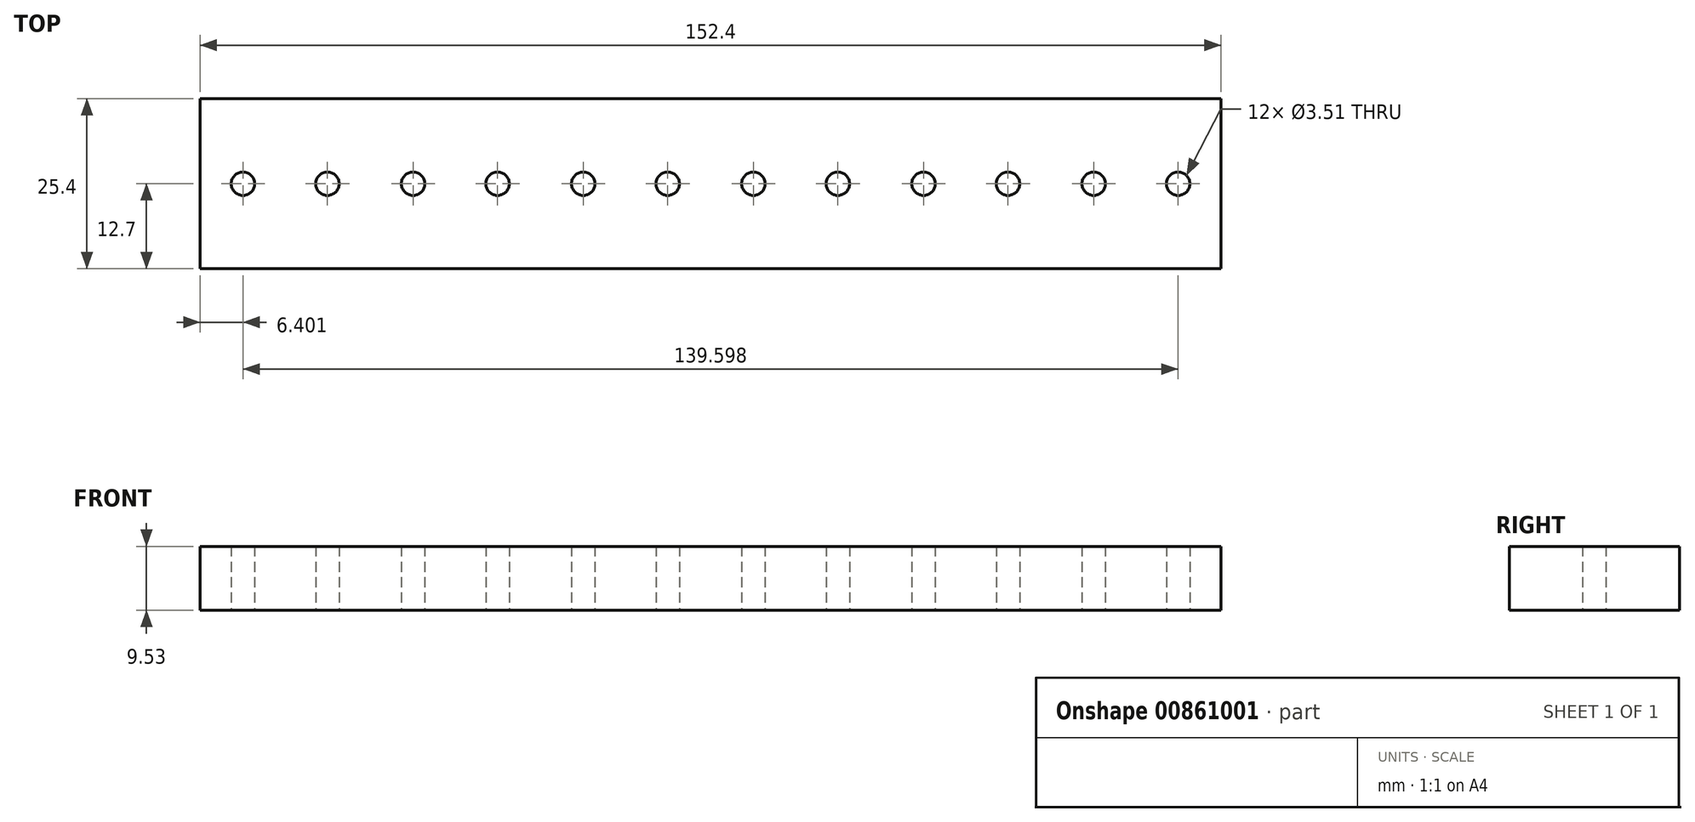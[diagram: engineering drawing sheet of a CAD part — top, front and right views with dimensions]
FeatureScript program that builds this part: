
annotation { "Feature Type Name" : "Feature", "Feature Type Description" : "" }
export const myFeature = defineFeature(function(context is Context, id is Id, definition is map)
    precondition{}
    {
        {
            var Q0;
            Q0=qCreatedBy(makeId("Top.planeOp"),FACE);
            var sketch = newSketch(context, id + "F0", { "sketchPlane" : qUnion([Q0])});
            skLineSegment(sketch, "E0.bottom", {"start": v(0, 0) * mm, "end": v(152.4, 0) * mm});
            skLineSegment(sketch, "E0.top", {"start": v(0, 25.4) * mm, "end": v(152.4, 25.4) * mm});
            skLineSegment(sketch, "E0.left", {"start": v(0, 0) * mm, "end": v(0, 25.4) * mm});
            skLineSegment(sketch, "E0.right", {"start": v(152.4, 0) * mm, "end": v(152.4, 25.4) * mm});
            skLineSegment(sketch, "E1", {"start": v(12.7, 25.4) * mm, "end": v(12.7, 0) * mm, "construction": true});
            skLineSegment(sketch, "E2", {"start": v(0, 12.7) * mm, "end": v(152.4, 12.7) * mm, "construction": true});
            skCircle(sketch, "E3", {"center": v(6.4, 12.7) * mm, "radius": 1.75 * mm});
            skLineSegment(sketch, "E4.direction1", {"start": v(6.4, 12.7) * mm, "end": v(19.2, 12.7) * mm, "construction": true});
            skCircle(sketch, "E5.MirrorC", {"center": v(19, 12.7) * mm, "radius": 1.75 * mm});
            skCircle(sketch, "E6.1.0.0", {"center": v(31.8, 12.7) * mm, "radius": 1.75 * mm});
            skLineSegment(sketch, "E6.1.0.1", {"start": v(38.1, 25.4) * mm, "end": v(38.1, 0) * mm, "construction": true});
            skCircle(sketch, "E6.1.0.2", {"center": v(44.4, 12.7) * mm, "radius": 1.75 * mm});
            skCircle(sketch, "E6.2.0.0", {"center": v(57.2, 12.7) * mm, "radius": 1.75 * mm});
            skLineSegment(sketch, "E6.2.0.1", {"start": v(63.5, 25.4) * mm, "end": v(63.5, 0) * mm, "construction": true});
            skCircle(sketch, "E6.2.0.2", {"center": v(69.8, 12.7) * mm, "radius": 1.75 * mm});
            skCircle(sketch, "E6.3.0.0", {"center": v(82.6, 12.7) * mm, "radius": 1.75 * mm});
            skLineSegment(sketch, "E6.3.0.1", {"start": v(88.9, 25.4) * mm, "end": v(88.9, 0) * mm, "construction": true});
            skCircle(sketch, "E6.3.0.2", {"center": v(95.2, 12.7) * mm, "radius": 1.75 * mm});
            skCircle(sketch, "E6.4.0.0", {"center": v(108, 12.7) * mm, "radius": 1.75 * mm});
            skLineSegment(sketch, "E6.4.0.1", {"start": v(114.3, 25.4) * mm, "end": v(114.3, 0) * mm, "construction": true});
            skCircle(sketch, "E6.4.0.2", {"center": v(120.6, 12.7) * mm, "radius": 1.75 * mm});
            skCircle(sketch, "E6.5.0.0", {"center": v(133.4, 12.7) * mm, "radius": 1.75 * mm});
            skLineSegment(sketch, "E6.5.0.1", {"start": v(139.7, 25.4) * mm, "end": v(139.7, 0) * mm, "construction": true});
            skCircle(sketch, "E6.5.0.2", {"center": v(146, 12.7) * mm, "radius": 1.75 * mm});
            skLineSegment(sketch, "E6.direction1", {"start": v(6.4, 12.7) * mm, "end": v(31.8, 12.7) * mm, "construction": true});
            skSolve(sketch);
        }
        {
            var Q0;
            Q0=makeQuery(id+"F0.imprint","IMPRINT",FACE,{"disambiguationData":[TD([[makeQuery(id+"F0.imprint","IMPRINT",EDGE,{"derivedFrom":sQuery(id+"F0.wireOp",EDGE,"E0.bottom")}),1.0]])]});
            extrude(context, id + "F1", {"entities" : qUnion([Q0]), "depth" : 9.52 * mm, "offsetDistance" : 25.4 * mm});
        }
    });
